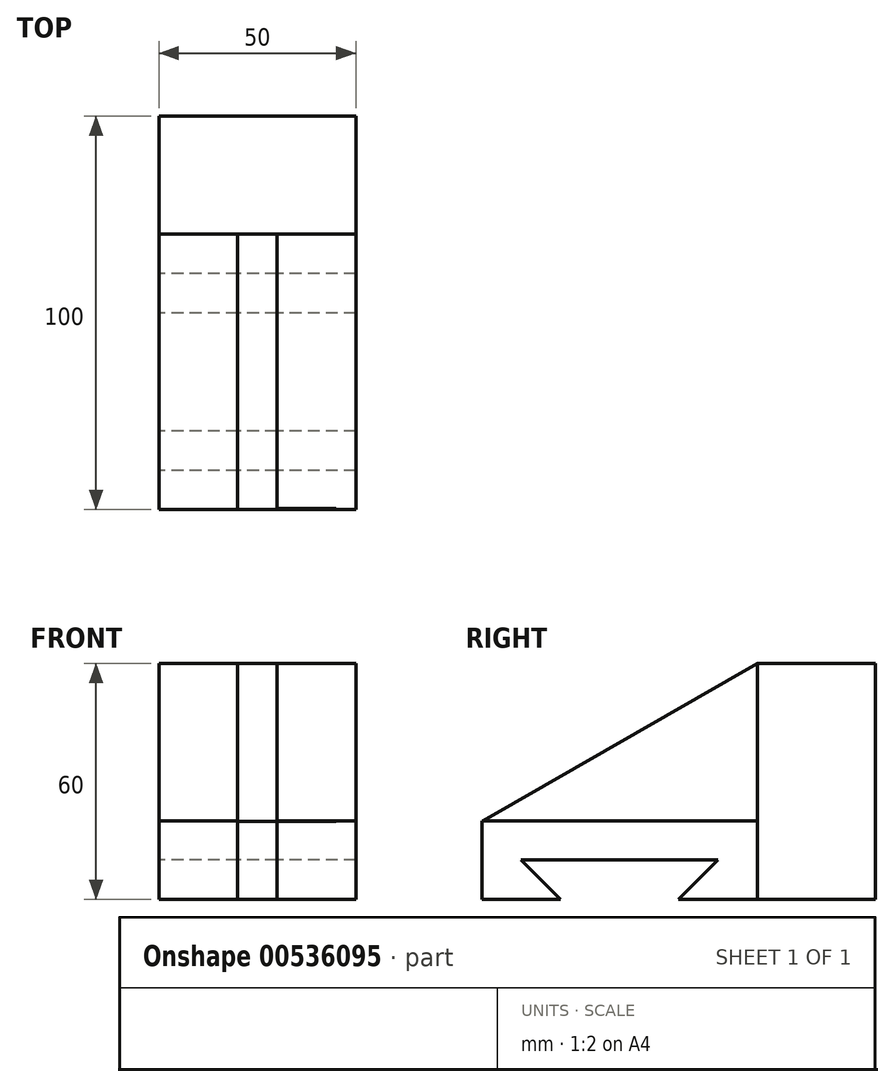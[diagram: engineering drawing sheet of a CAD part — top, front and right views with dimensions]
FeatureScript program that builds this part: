
annotation { "Feature Type Name" : "Feature", "Feature Type Description" : "" }
export const myFeature = defineFeature(function(context is Context, id is Id, definition is map)
    precondition{}
    {
        {
            var Q0;
            Q0=qCreatedBy(makeId("Top.planeOp"),FACE);
            var sketch = newSketch(context, id + "F0", { "sketchPlane" : qUnion([Q0])});
            skLineSegment(sketch, "E0.bottom", {"start": v(-20, 67.26) * mm, "end": v(30, 67.26) * mm});
            skLineSegment(sketch, "E0.top", {"start": v(-20, -32.74) * mm, "end": v(30, -32.74) * mm});
            skLineSegment(sketch, "E0.left", {"start": v(-20, 67.26) * mm, "end": v(-20, -32.74) * mm});
            skLineSegment(sketch, "E0.right", {"start": v(30, 67.26) * mm, "end": v(30, -32.74) * mm});
            skLineSegment(sketch, "E1", {"start": v(30, 67.26) * mm, "end": v(30, 37.26) * mm});
            skLineSegment(sketch, "E2", {"start": v(30, 37.26) * mm, "end": v(-20, 37.26) * mm});
            skLineSegment(sketch, "E3", {"start": v(5, 37.26) * mm, "end": v(10, 37.26) * mm});
            skLineSegment(sketch, "E4", {"start": v(10, 37.26) * mm, "end": v(0, 37.26) * mm});
            skLineSegment(sketch, "E5", {"start": v(0, 37.26) * mm, "end": v(0, -32.74) * mm});
            skLineSegment(sketch, "E6", {"start": v(10, 37.26) * mm, "end": v(10, -32.74) * mm});
            skPoint(sketch, "E6.endSnap0", {"position": v(5, -32.74) * mm});
            skSolve(sketch);
        }
        {
            var Q0;
            {var subQ3=sQuery(id+"F0.wireOp",EDGE,"E5");Q0=makeQuery(id+"F0.imprint","IMPRINT",FACE,{"disambiguationData":[TD([[makeQuery(id+"F0.imprint","IMPRINT",EDGE,{"derivedFrom":subQ3}),-1.0]])]});}
            var Q1;
            {var subQ0=sQuery(id+"F0.wireOp",EDGE,"E0.right");Q1=makeQuery(id+"F0.imprint","IMPRINT",FACE,{"disambiguationData":[TD([[makeQuery(id+"F0.imprint","IMPRINT",EDGE,{"derivedFrom":subQ0}),-1.0]])]});}
            extrude(context, id + "F1", {"entities" : qUnion([Q0, Q1]), "depth" : 20 * mm, "offsetDistance" : 25 * mm});
        }
        {
            var Q0;
            {var subQ5=sQuery(id+"F0.wireOp",EDGE,"E0.bottom");Q0=makeQuery(id+"F0.imprint","IMPRINT",FACE,{"disambiguationData":[TD([[makeQuery(id+"F0.imprint","IMPRINT",EDGE,{"derivedFrom":subQ5}),-1.0]])]});}
            extrude(context, id + "F2", {"entities" : qUnion([Q0]), "depth" : 60 * mm, "offsetDistance" : 25 * mm});
        }
        {
            var Q0;
            {var subQ0=sQuery(id+"F0.wireOp",EDGE,"E5");Q0=makeQuery(id+"F0.imprint","IMPRINT",FACE,{"disambiguationData":[TD([[makeQuery(id+"F0.imprint","IMPRINT",EDGE,{"derivedFrom":subQ0}),1.0]])]});}
            extrude(context, id + "F3", {"entities" : qUnion([Q0]), "depth" : 60 * mm, "offsetDistance" : 25 * mm});
        }
        {
            var Q0;
            Q0=makeQuery(id+"F3.opExtrude","SWEPT_FACE",FACE,{"disambiguationData":[OSD([sQuery(id+"F0.wireOp",EDGE,"E5")])]});
            var sketch = newSketch(context, id + "F4", { "sketchPlane" : qUnion([Q0])});
            skLineSegment(sketch, "E7", {"start": v(-37.26, 60) * mm, "end": v(32.74, 19.83) * mm});
            skSolve(sketch);
        }
        {
            var Q0;
            {var subQ0=sQuery(id+"F4.wireOp",EDGE,"E7");Q0=makeQuery(id+"F4.imprint","IMPRINT",FACE,{"disambiguationData":[TD([[makeQuery(id+"F4.imprint","IMPRINT",EDGE,{"derivedFrom":subQ0}),1.0]])]});}
            extrude(context, id + "F5", {"entities" : qUnion([Q0]), "operationType" : NewBodyOperationType.REMOVE, "oppositeDirection" : true, "depth" : 25 * mm, "offsetDistance" : 25 * mm});
        }
        {
            var Q0;
            Q0=makeQuery(id+"F1.opExtrude","SWEPT_FACE",FACE,{"disambiguationData":[OSD([sQuery(id+"F0.wireOp",EDGE,"E0.left")])]});
            var sketch = newSketch(context, id + "F6", { "sketchPlane" : qUnion([Q0])});
            skLineSegment(sketch, "E8", {"start": v(32.74, 0) * mm, "end": v(12.74, 0) * mm});
            skLineSegment(sketch, "E9", {"start": v(12.74, 0) * mm, "end": v(-17.26, 0) * mm});
            skLineSegment(sketch, "E10", {"start": v(-17.26, 0) * mm, "end": v(-17.26, 10) * mm});
            skLineSegment(sketch, "E11", {"start": v(-17.26, 10) * mm, "end": v(12.74, 10) * mm});
            skLineSegment(sketch, "E12", {"start": v(12.74, 10) * mm, "end": v(12.74, 0) * mm});
            skLineSegment(sketch, "E13", {"start": v(12.74, 0) * mm, "end": v(28.4, 15.66) * mm});
            skLineSegment(sketch, "E14", {"start": v(-17.26, 0) * mm, "end": v(-31.03, 13.78) * mm});
            skLineSegment(sketch, "E15", {"start": v(22.74, 10) * mm, "end": v(-27.26, 10) * mm});
            skSolve(sketch);
        }
        {
            var Q0;
            Q0=makeQuery(id+"F6.imprint","IMPRINT",FACE,{"disambiguationData":[TD([[makeQuery(id+"F6.imprint","IMPRINT",EDGE,{"derivedFrom":sQuery(id+"F6.wireOp",EDGE,"E9")}),1.0]])]});
            var Q1;
            {var subQ0=sQuery(id+"F6.wireOp",EDGE,"E10");Q1=makeQuery(id+"F6.imprint","IMPRINT",FACE,{"disambiguationData":[TD([[makeQuery(id+"F6.imprint","IMPRINT",EDGE,{"derivedFrom":subQ0}),1.0]])]});}
            var Q2;
            {var subQ0=sQuery(id+"F6.wireOp",EDGE,"E12");Q2=makeQuery(id+"F6.imprint","IMPRINT",FACE,{"disambiguationData":[TD([[makeQuery(id+"F6.imprint","IMPRINT",EDGE,{"derivedFrom":subQ0}),1.0]])]});}
            extrude(context, id + "F7", {"entities" : qUnion([Q0, Q1, Q2]), "operationType" : NewBodyOperationType.REMOVE, "oppositeDirection" : true, "depth" : 107 * mm, "offsetDistance" : 25 * mm});
        }
    });
